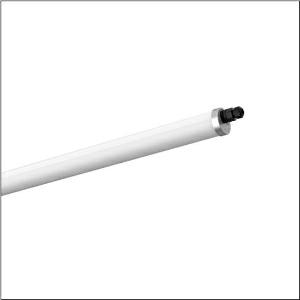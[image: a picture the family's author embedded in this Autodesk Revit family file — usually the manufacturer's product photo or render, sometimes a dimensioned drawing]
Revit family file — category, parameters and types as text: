
# Revit family: monsun_r__31_tube_51ft10dn4a0a_ff33
name_source: partatom
category: Lighting Fixtures
units: mm (PartAtom-declared; Revit-internal decimal feet)

## family parameters
Cut with Voids When Loaded = No
Host = Face
Light Source = No
Part Type = Normal
Room Calculation Point = No
Round Connector Dimension = Use Diameter
Shared = No

## types (1)
- Monsun® 31 Tube (1 x LED, 10000 lm, 58 W, 4000K)
    Apparent Load = 58 VA
    CIE Flux Codes = 42 71 90 91 100
    Color Rendering = 80
    Color Temperature = 4000K
    Default Elevation = 1800 mm
    Description = Monsun® 31 Tube, tubular luminaire, primary optical cover: diffuser, of PMMA, light emission: direct distribution, primary light characteristic: symmetric, installation type: suspended mounting, surface-mounted, LED, rated luminous flux: 10.000lm, luminous efficacy: 160lm/W, light colour: 840, colour temperature: 4000K, with with 1 terminal, 5-pole, max. 2.5mm², through-wiring: 5x 1.5mm², mains connection: 220..240V, AC, 50/60Hz, rated input power: 58W, housing, cylindrical, of PMMA, semi-transparent, matt white, with luminaire and ceiling fastening, V4A, mounting with brackets of stainless steel, length: 1.570mm, diameter: 75mm, end cap, of stainless steel (V4A), protection rating (complete): IP67/IP69K, insulation class (complete): insulation class I (protective earthing), certification: CE, UKCA, impact resistance: IK07, permissible operating ambient temperature: -20..+40°C, corresponds to IFS (International Featured Standards) requirements for safety and quality in the food industry, usage in unprotected outdoor area possible with horizontal mounting, contact your sales advisor before using the luminaires in applications with unclear chemical exposure, large temperature fluctuations or condensation-forming humidity, packaging unit: 1 piece
    Height = 83 mm
    Lamp = 1 x LED
    Lamp Light Flux = 10000 lm
    Lamp Power = 58 W
    Lamp count = 1
    Length = 1570 mm
    Luminous efficacy = 172 lm/W
    Manufacturer = Siteco
    ModVariant = No
    Model = 51FT10DN4A0A
    Mounting Place = Ceiling
    Mounting Type = Pendant
    Number of Poles = 1
    OnlyDefault = Yes
    Power Factor = 1
    Product Name = Monsun® 31 Tube
    Product group = tubular luminaire
    ProductGroupID = 906
    Protection Class = Protection class I
    RLX_Detail_Level = 1
    RLX_Emergency_Light_Flux = 0 lm
    RLX_Emergency_Type = 0
    RLX_Emergency_Type_DB = No
    RlxData = <blob elided: 25377 chars, md5=e3421067>
    Socket = socket
    Standby Power = 0 W
    System Light Flux = 10000 lm
    System Power = 58 W
    Type Comments = Product without accessories
    Type Image = l_1228461.jpg
    URL = http://relux.com
    VarID = ---
    Voltage = 0 V
    Weight = 0.00 kg
    Width = 75 mm

## geometry (parser evidence)
native form markers: Blend x4, Sweep x13
no freeform markers — native parametric forms only
